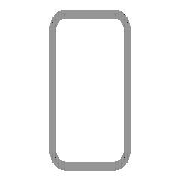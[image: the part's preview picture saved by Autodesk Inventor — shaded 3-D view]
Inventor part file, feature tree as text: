
AUTODESK INVENTOR PART (.ipt)
format: ipt  version: 2025 (Build 290162010, 162A)  size: 135,168 bytes
history: native  units: mm (DEFAULTED — no unit token found)
features: other x4, sketch x1, plane x1
ambient origin geometry x8: Origin, YZ Plane, XZ Plane, XY Plane, X Axis, Y Axis, Z Axis, Center Point
bodies: Solid1 (feature_tree), Body (feature_tree)
feature tree (6):
  parser-record x1  (decoder bookkeeping rows leaked as tree rows — omitted from the tree; the rows remain in map.json)
  other  "Driven Length"
  other  "Start Plane"
  other  "End Plane"
  sketch  "Sketch3"  dims[d3=5000.0mm d4=0.0mm d7=6.0mm d9=40.0mm d11=60.0mm d12=3.0mm d13=-0.0mm d14=5000.0mm d15=20.0mm d16=30.0mm d17=90.0deg d18=5000.0mm]
  plane  "Work Plane3"
